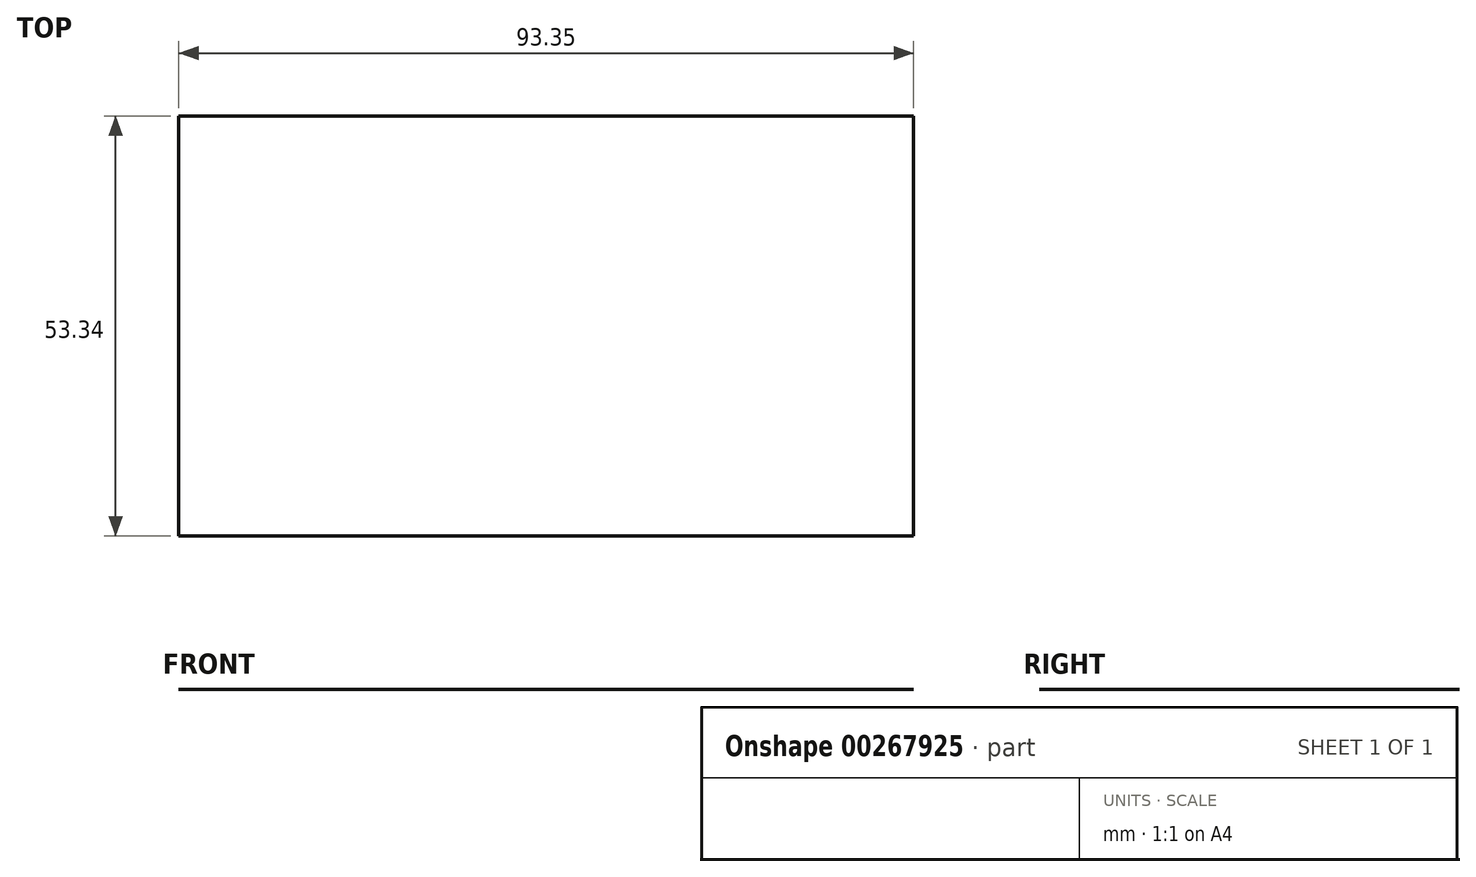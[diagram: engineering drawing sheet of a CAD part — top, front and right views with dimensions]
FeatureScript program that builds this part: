
annotation { "Feature Type Name" : "Feature", "Feature Type Description" : "" }
export const myFeature = defineFeature(function(context is Context, id is Id, definition is map)
    precondition{}
    {
        {
            var Q0;
            Q0=qCreatedBy(makeId("Front.planeOp"),FACE);
            var sketch = newSketch(context, id + "F0", { "sketchPlane" : qUnion([Q0])});
            skLineSegment(sketch, "E0.bottom", {"start": v(-78.89, 53.43) * mm, "end": v(14.46, 53.43) * mm});
            skLineSegment(sketch, "E0.top", {"start": v(-78.89, -22.47) * mm, "end": v(14.46, -22.47) * mm});
            skLineSegment(sketch, "E0.left", {"start": v(-78.89, 53.43) * mm, "end": v(-78.89, -22.47) * mm});
            skLineSegment(sketch, "E0.right", {"start": v(14.46, 53.43) * mm, "end": v(14.46, -22.47) * mm});
            skSolve(sketch);
        }
        {
            var Q0;
            Q0=sQuery(id+"F0.wireOp",EDGE,"E0.bottom");
            extrude(context, id + "F1", {"bodyType" : ToolBodyType.SURFACE, "surfaceEntities" : qUnion([Q0]), "depth" : 53.34 * mm});
        }
    });
